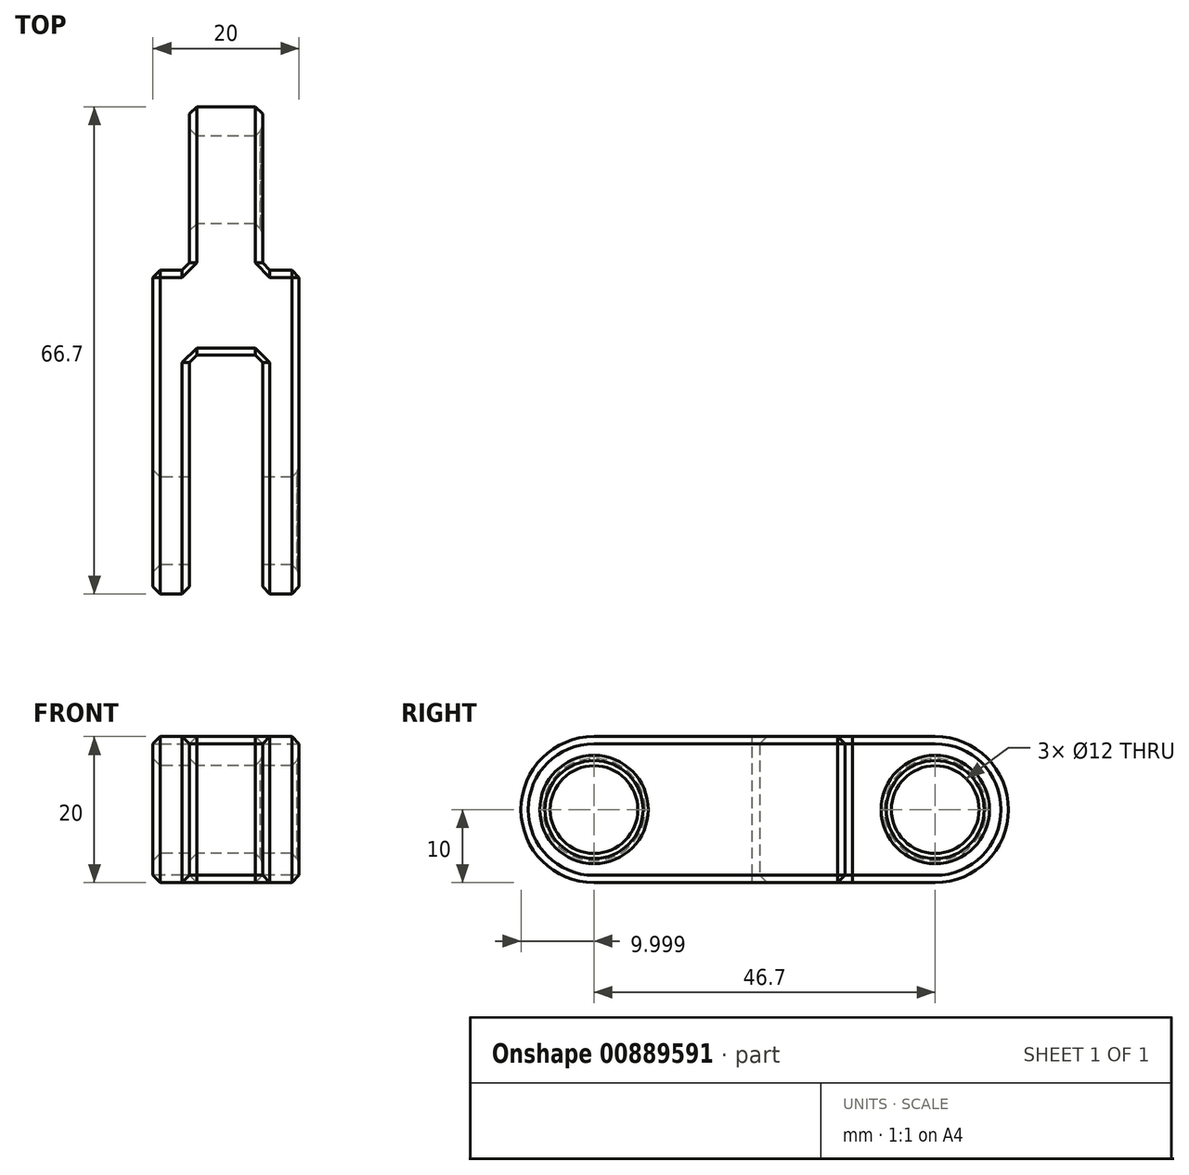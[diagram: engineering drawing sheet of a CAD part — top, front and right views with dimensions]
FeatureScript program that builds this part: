
annotation { "Feature Type Name" : "Feature", "Feature Type Description" : "" }
export const myFeature = defineFeature(function(context is Context, id is Id, definition is map)
    precondition{}
    {
        {
            var Q0;
            Q0=qCreatedBy(makeId("Top.planeOp"),FACE);
            var sketch = newSketch(context, id + "F0", { "sketchPlane" : qUnion([Q0])});
            skLineSegment(sketch, "E0", {"start": v(-10, 15.26) * mm, "end": v(-10, -26.74) * mm});
            skLineSegment(sketch, "E1", {"start": v(-10, -26.74) * mm, "end": v(-5, -26.74) * mm});
            skLineSegment(sketch, "E2", {"start": v(-5, -26.74) * mm, "end": v(-5, 5.94) * mm});
            skLineSegment(sketch, "E3", {"start": v(-5, 5.94) * mm, "end": v(5, 5.94) * mm});
            skLineSegment(sketch, "E4", {"start": v(5, 5.94) * mm, "end": v(5, -26.74) * mm});
            skLineSegment(sketch, "E5", {"start": v(5, -26.74) * mm, "end": v(10, -26.74) * mm});
            skLineSegment(sketch, "E6", {"start": v(10, -26.74) * mm, "end": v(10, 15.26) * mm});
            skLineSegment(sketch, "E7", {"start": v(-10, 15.26) * mm, "end": v(10, 15.26) * mm});
            skSolve(sketch);
        }
        {
            var Q0;
            Q0=makeQuery(id+"F0.imprint","IMPRINT",FACE,{"disambiguationData":[TD([[makeQuery(id+"F0.imprint","IMPRINT",EDGE,{"derivedFrom":sQuery(id+"F0.wireOp",EDGE,"E0")}),1.0]])]});
            extrude(context, id + "F1", {"entities" : qUnion([Q0]), "depth" : 20 * mm, "offsetDistance" : 25 * mm});
        }
        {
            var Q0;
            Q0=makeQuery(id+"F1.opExtrude","CAP_EDGE",EDGE,{"disambiguationData":[OSD([sQuery(id+"F0.wireOp",EDGE,"E1")])],"isStart":false});
            var Q1;
            Q1=makeQuery(id+"F1.opExtrude","CAP_EDGE",EDGE,{"disambiguationData":[OSD([sQuery(id+"F0.wireOp",EDGE,"E5")])],"isStart":false});
            var Q2;
            Q2=makeQuery(id+"F1.opExtrude","CAP_EDGE",EDGE,{"disambiguationData":[OSD([sQuery(id+"F0.wireOp",EDGE,"E1")])],"isStart":true});
            var Q3;
            Q3=makeQuery(id+"F1.opExtrude","CAP_EDGE",EDGE,{"disambiguationData":[OSD([sQuery(id+"F0.wireOp",EDGE,"E5")])],"isStart":true});
            fillet(context, id + "F2", {"entities" : qUnion([Q0, Q1, Q2, Q3]), "radius" : 10 * mm, "tangentPropagation" : true, "allowEdgeOverflow" : false});
        }
        {
            var Q0;
            Q0=makeQuery(id+"F1.opExtrude","SWEPT_FACE",FACE,{"disambiguationData":[OSD([sQuery(id+"F0.wireOp",EDGE,"E0")])]});
            var sketch = newSketch(context, id + "F3", { "sketchPlane" : qUnion([Q0])});
            skCircle(sketch, "E8", {"center": v(16.74, 10) * mm, "radius": 6 * mm});
            skSolve(sketch);
        }
        {
            var Q0;
            Q0=makeQuery(id+"F3.imprint","IMPRINT",FACE,{"disambiguationData":[TD([[makeQuery(id+"F3.imprint","IMPRINT",EDGE,{"derivedFrom":sQuery(id+"F3.wireOp",EDGE,"E8")}),1.0]])]});
            extrude(context, id + "F4", {"entities" : qUnion([Q0]), "operationType" : NewBodyOperationType.REMOVE, "endBound" : BoundingType.THROUGH_ALL, "oppositeDirection" : true, "depth" : 25 * mm, "offsetDistance" : 25 * mm});
        }
        {
            var Q0;
            Q0=makeQuery(id+"F4.boolean.opBoolean","COPY",EDGE,{"derivedFrom":makeQuery(id+"F4.opExtrude","CAP_EDGE",EDGE,{"disambiguationData":[OSD([sQuery(id+"F3.wireOp",EDGE,"E8")])],"isStart":true})});
            var Q1;
            Q1=makeQuery(id+"F4.boolean.opBoolean","INTERSECT",EDGE,{"derivedFrom":[makeQuery(id+"F1.opExtrude","SWEPT_FACE",FACE,{"disambiguationData":[OSD([sQuery(id+"F0.wireOp",EDGE,"E6")])]}),makeQuery(id+"F4.opExtrude","SWEPT_FACE",FACE,{"disambiguationData":[OSD([sQuery(id+"F3.wireOp",EDGE,"E8")])]})]});
            chamfer(context, id + "F5", {"entities" : qUnion([Q0, Q1]), "width" : 1 * mm, "tangentPropagation" : true});
        }
        {
            var Q0;
            Q0=makeQuery(id+"F1.opExtrude","SWEPT_FACE",FACE,{"disambiguationData":[OSD([sQuery(id+"F0.wireOp",EDGE,"E7")])]});
            extrude(context, id + "F6", {"entities" : qUnion([Q0]), "operationType" : NewBodyOperationType.ADD, "depth" : 24.7 * mm, "offsetDistance" : 25 * mm});
        }
        {
            var Q0;
            {var subQ0=sQuery(id+"F0.wireOp",EDGE,"E7");Q0=makeQuery(id+"F6.boolean.opBoolean","MERGE",FACE,{"derivedFrom":[makeQuery(id+"F1.opExtrude","CAP_FACE",FACE,{"disambiguationData":[OSD([sQuery(id+"F0.wireOp",EDGE,"E0"),sQuery(id+"F0.wireOp",EDGE,"E1"),sQuery(id+"F0.wireOp",EDGE,"E2"),sQuery(id+"F0.wireOp",EDGE,"E3"),sQuery(id+"F0.wireOp",EDGE,"E4"),sQuery(id+"F0.wireOp",EDGE,"E5"),sQuery(id+"F0.wireOp",EDGE,"E6"),subQ0])],"isStart":false}),makeQuery(id+"F6.opExtrude","SWEPT_FACE",FACE,{"disambiguationData":[OSD([subQ0]),TDD([makeQuery(id+"F1.opExtrude","CAP_EDGE",EDGE,{"disambiguationData":[OSD([subQ0])],"isStart":false})])]})]});}
            var sketch = newSketch(context, id + "F7", { "sketchPlane" : qUnion([Q0])});
            skLineSegment(sketch, "E9", {"start": v(-10, 17.6) * mm, "end": v(-5, 17.6) * mm});
            skLineSegment(sketch, "E10", {"start": v(-5, 17.6) * mm, "end": v(-5, 39.96) * mm});
            skLineSegment(sketch, "E11", {"start": v(-5, 39.96) * mm, "end": v(5, 39.96) * mm});
            skLineSegment(sketch, "E12", {"start": v(5, 39.96) * mm, "end": v(5, 17.6) * mm});
            skLineSegment(sketch, "E13", {"start": v(5, 17.6) * mm, "end": v(10, 17.6) * mm});
            skLineSegment(sketch, "E14", {"start": v(10, 17.6) * mm, "end": v(10, 70.93) * mm});
            skLineSegment(sketch, "E15", {"start": v(10, 70.93) * mm, "end": v(-10, 70.93) * mm});
            skLineSegment(sketch, "E16", {"start": v(-10, 70.93) * mm, "end": v(-10, 17.6) * mm});
            skSolve(sketch);
        }
        {
            var Q0;
            {var subQ0=sQuery(id+"F7.wireOp",EDGE,"E9");Q0=makeQuery(id+"F7.imprint","IMPRINT",FACE,{"disambiguationData":[TD([[makeQuery(id+"F7.imprint","IMPRINT",EDGE,{"derivedFrom":subQ0}),1.0]])]});}
            var Q1;
            {var subQ0=sQuery(id+"F7.wireOp",EDGE,"E12");Q1=makeQuery(id+"F7.imprint","IMPRINT",FACE,{"disambiguationData":[TD([[makeQuery(id+"F7.imprint","IMPRINT",EDGE,{"derivedFrom":subQ0}),1.0]])]});}
            extrude(context, id + "F8", {"entities" : qUnion([Q0, Q1]), "operationType" : NewBodyOperationType.REMOVE, "oppositeDirection" : true, "depth" : 25 * mm, "offsetDistance" : 25 * mm});
        }
        {
            var Q0;
            {var subQ0=sQuery(id+"F0.wireOp",EDGE,"E7");Q0=makeQuery(id+"F6.opExtrude","CAP_EDGE",EDGE,{"disambiguationData":[OSD([subQ0]),TDD([makeQuery(id+"F1.opExtrude","CAP_EDGE",EDGE,{"disambiguationData":[OSD([subQ0])],"isStart":false})])],"isStart":false});}
            var Q1;
            {var subQ0=sQuery(id+"F0.wireOp",EDGE,"E7");Q1=makeQuery(id+"F6.opExtrude","CAP_EDGE",EDGE,{"disambiguationData":[OSD([subQ0]),TDD([makeQuery(id+"F1.opExtrude","CAP_EDGE",EDGE,{"disambiguationData":[OSD([subQ0])],"isStart":true})])],"isStart":false});}
            fillet(context, id + "F9", {"entities" : qUnion([Q0, Q1]), "radius" : 10 * mm, "tangentPropagation" : true, "allowEdgeOverflow" : false});
        }
        {
            var Q0;
            Q0=makeQuery(id+"F8.boolean.opBoolean","COPY",FACE,{"derivedFrom":makeQuery(id+"F8.opExtrude","SWEPT_FACE",FACE,{"disambiguationData":[OSD([sQuery(id+"F7.wireOp",EDGE,"E10")])]})});
            var sketch = newSketch(context, id + "F10", { "sketchPlane" : qUnion([Q0])});
            skCircle(sketch, "E17", {"center": v(-29.96, 10) * mm, "radius": 6 * mm});
            skSolve(sketch);
        }
        {
            var Q0;
            Q0=makeQuery(id+"F10.imprint","IMPRINT",FACE,{"disambiguationData":[TD([[makeQuery(id+"F10.imprint","IMPRINT",EDGE,{"derivedFrom":sQuery(id+"F10.wireOp",EDGE,"E17")}),1.0]])]});
            extrude(context, id + "F11", {"entities" : qUnion([Q0]), "operationType" : NewBodyOperationType.REMOVE, "oppositeDirection" : true, "depth" : 25 * mm, "offsetDistance" : 25 * mm});
        }
        {
            var Q0;
            Q0=makeQuery(id+"F11.boolean.opBoolean","COPY",EDGE,{"derivedFrom":makeQuery(id+"F11.opExtrude","CAP_EDGE",EDGE,{"disambiguationData":[OSD([sQuery(id+"F10.wireOp",EDGE,"E17")])],"isStart":true})});
            var Q1;
            Q1=makeQuery(id+"F11.boolean.opBoolean","INTERSECT",EDGE,{"derivedFrom":[makeQuery(id+"F8.boolean.opBoolean","COPY",FACE,{"derivedFrom":makeQuery(id+"F8.opExtrude","SWEPT_FACE",FACE,{"disambiguationData":[OSD([sQuery(id+"F7.wireOp",EDGE,"E12")])]})}),makeQuery(id+"F11.opExtrude","SWEPT_FACE",FACE,{"disambiguationData":[OSD([sQuery(id+"F10.wireOp",EDGE,"E17")])]})]});
            chamfer(context, id + "F12", {"entities" : qUnion([Q0, Q1]), "width" : 1 * mm, "tangentPropagation" : true});
        }
        {
            var Q0;
            {var subQ0=sQuery(id+"F0.wireOp",EDGE,"E0");Q0=makeQuery(id+"F6.boolean.opBoolean","MERGE",FACE,{"derivedFrom":[makeQuery(id+"F1.opExtrude","SWEPT_FACE",FACE,{"disambiguationData":[OSD([subQ0])]}),makeQuery(id+"F6.opExtrude","SWEPT_FACE",FACE,{"disambiguationData":[OSD([subQ0,sQuery(id+"F0.wireOp",EDGE,"E7")])]})]});}
            var Q1;
            {var subQ0=sQuery(id+"F0.wireOp",EDGE,"E6");Q1=makeQuery(id+"F6.boolean.opBoolean","MERGE",FACE,{"derivedFrom":[makeQuery(id+"F1.opExtrude","SWEPT_FACE",FACE,{"disambiguationData":[OSD([subQ0])]}),makeQuery(id+"F6.opExtrude","SWEPT_FACE",FACE,{"disambiguationData":[OSD([subQ0,sQuery(id+"F0.wireOp",EDGE,"E7")])]})]});}
            var Q2;
            Q2=makeQuery(id+"F8.boolean.opBoolean","COPY",FACE,{"derivedFrom":makeQuery(id+"F8.opExtrude","SWEPT_FACE",FACE,{"disambiguationData":[OSD([sQuery(id+"F7.wireOp",EDGE,"E9")])]})});
            var Q3;
            Q3=makeQuery(id+"F8.boolean.opBoolean","COPY",FACE,{"derivedFrom":makeQuery(id+"F8.opExtrude","SWEPT_FACE",FACE,{"disambiguationData":[OSD([sQuery(id+"F7.wireOp",EDGE,"E10")])]})});
            var Q4;
            Q4=makeQuery(id+"F8.boolean.opBoolean","COPY",FACE,{"derivedFrom":makeQuery(id+"F8.opExtrude","SWEPT_FACE",FACE,{"disambiguationData":[OSD([sQuery(id+"F7.wireOp",EDGE,"E12")])]})});
            var Q5;
            Q5=makeQuery(id+"F8.boolean.opBoolean","COPY",FACE,{"derivedFrom":makeQuery(id+"F8.opExtrude","SWEPT_FACE",FACE,{"disambiguationData":[OSD([sQuery(id+"F7.wireOp",EDGE,"E13")])]})});
            var Q6;
            Q6=makeQuery(id+"F1.opExtrude","SWEPT_FACE",FACE,{"disambiguationData":[OSD([sQuery(id+"F0.wireOp",EDGE,"E3")])]});
            chamfer(context, id + "F13", {"entities" : qUnion([Q0, Q1, Q2, Q3, Q4, Q5, Q6]), "width" : 1 * mm, "tangentPropagation" : true});
        }
    });
